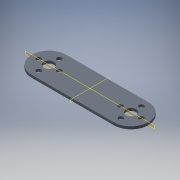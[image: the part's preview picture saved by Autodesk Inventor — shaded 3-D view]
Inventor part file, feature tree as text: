
AUTODESK INVENTOR PART (.ipt)
format: ipt  version: 2019 (Build 230136000, 136)  size: 151,040 bytes
history: native  units: in
note: dims shown in document units (in); Inventor stores cm internally (conversion verified against a paired STEP export)
features: other x15, plane x2, imported_body x1
ambient origin geometry x8: Origin, YZ Plane, XZ Plane, XY Plane, X Axis, Y Axis, Z Axis, Center Point
bodies: Body1 (feature_tree)
feature tree (18):
  other  "tetrix_739061_2012"
  other  "tetrix_739061_20121"
  other  "A_1"
  other  "A_2"
  other  "A_3"
  other  "A_4"
  other  "A_5"
  other  "A_6"
  other  "A_7"
  other  "A_8"
  other  "A_9"
  other  "A_10"
  other  "FRONT"
  other  "TOP"
  other  "RIGHT"
  plane  "Work Plane4"
  plane  "Work Plane5"
  imported_body  "Base1"
